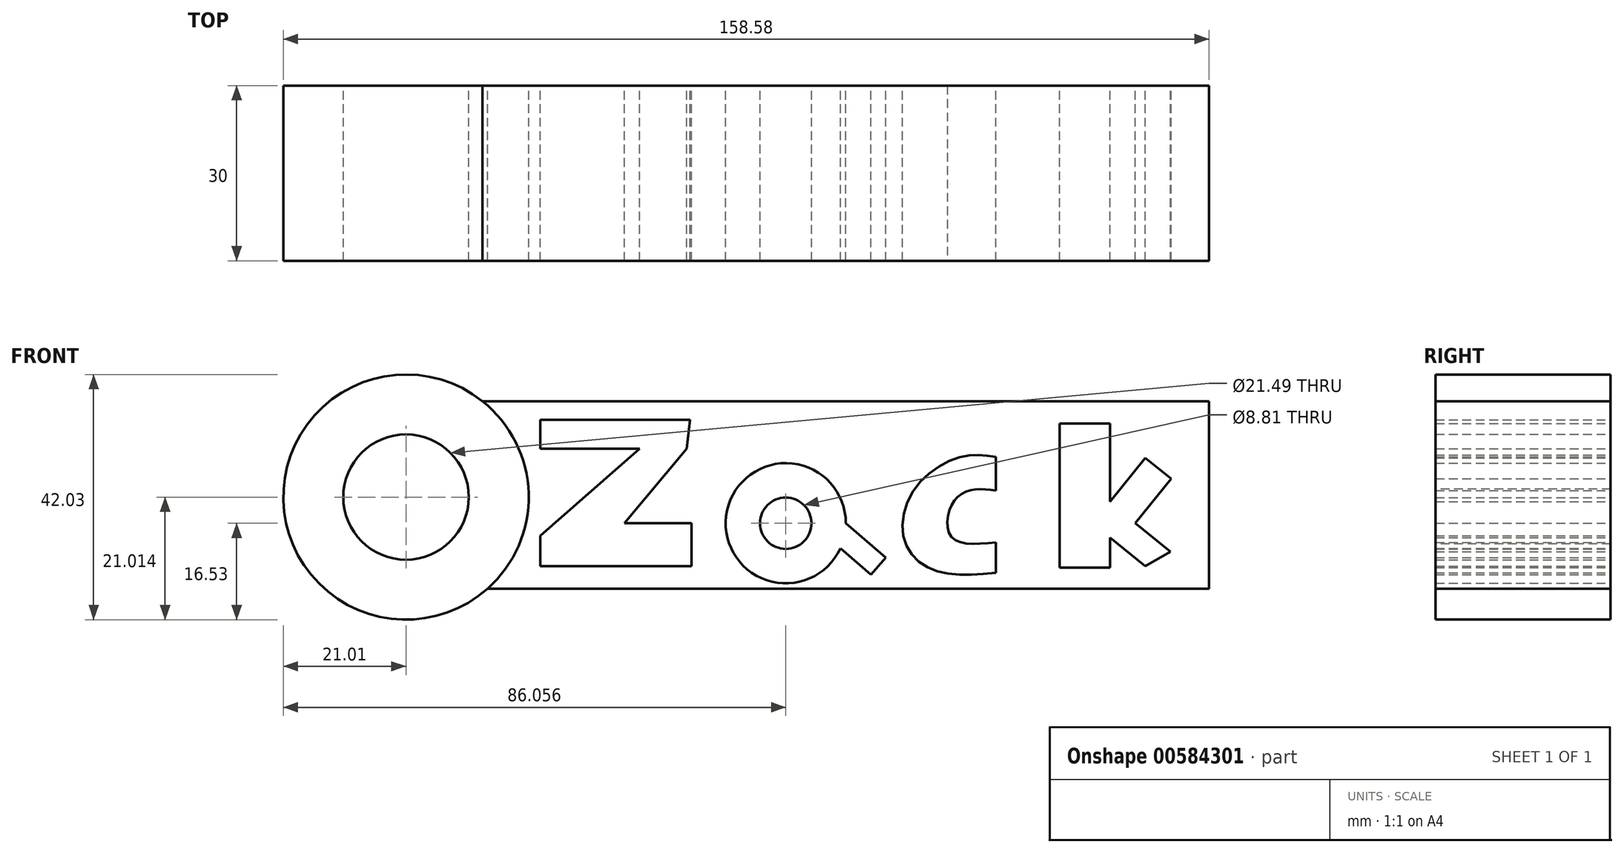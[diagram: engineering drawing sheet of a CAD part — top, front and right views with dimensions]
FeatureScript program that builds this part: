
annotation { "Feature Type Name" : "Feature", "Feature Type Description" : "" }
export const myFeature = defineFeature(function(context is Context, id is Id, definition is map)
    precondition{}
    {
        {
            var Q0;
            Q0=qCreatedBy(makeId("Front.planeOp"),FACE);
            var sketch = newSketch(context, id + "F0", { "sketchPlane" : qUnion([Q0])});
            skCircle(sketch, "E0", {"center": v(-82.17, 4.48) * mm, "radius": 21.01 * mm});
            skCircle(sketch, "E1", {"center": v(-82.17, 4.48) * mm, "radius": 10.75 * mm});
            skLineSegment(sketch, "E2", {"start": v(-69.1, 20.93) * mm, "end": v(55.4, 20.93) * mm});
            skLineSegment(sketch, "E3", {"start": v(-68.2, -11.21) * mm, "end": v(55.4, -11.21) * mm});
            skLineSegment(sketch, "E4", {"start": v(55.4, -11.21) * mm, "end": v(55.4, 20.93) * mm});
            skSolve(sketch);
        }
        {
            var Q0;
            {var subQ0=sQuery(id+"F0.wireOp",EDGE,"E2");Q0=makeQuery(id+"F0.imprint","IMPRINT",FACE,{"disambiguationData":[TD([[makeQuery(id+"F0.imprint","IMPRINT",EDGE,{"derivedFrom":subQ0}),-1.0]])]});}
            var sketch = newSketch(context, id + "F1", { "sketchPlane" : qUnion([Q0])});
            skLineSegment(sketch, "E5", {"start": v(-59.14, 17.7) * mm, "end": v(-59.14, 12.8) * mm});
            skLineSegment(sketch, "E6", {"start": v(-59.14, 12.8) * mm, "end": v(-42.16, 12.8) * mm});
            skLineSegment(sketch, "E7", {"start": v(-42.16, 12.8) * mm, "end": v(-59.14, -2.16) * mm});
            skLineSegment(sketch, "E8", {"start": v(-59.14, -2.16) * mm, "end": v(-59.14, -7.34) * mm});
            skPoint(sketch, "E9.end.orphan", {"position": v(-42.16, 0) * mm});
            skPoint(sketch, "E10.start.orphan", {"position": v(-34.1, 12.8) * mm});
            skPoint(sketch, "E11.end.orphan", {"position": v(-42.16, -7.34) * mm});
            skLineSegment(sketch, "E12", {"start": v(-59.14, -7.34) * mm, "end": v(-33.24, -7.34) * mm});
            skLineSegment(sketch, "E13", {"start": v(-33.24, -7.34) * mm, "end": v(-33.24, 0) * mm});
            skLineSegment(sketch, "E14", {"start": v(-33.24, 0) * mm, "end": v(-44.75, 0) * mm});
            skPoint(sketch, "E15.end.orphan", {"position": v(-30.65, 12.8) * mm});
            skLineSegment(sketch, "E16", {"start": v(-59.14, 17.7) * mm, "end": v(-33.53, 17.7) * mm});
            skLineSegment(sketch, "E17", {"start": v(-33.53, 17.7) * mm, "end": v(-34.1, 12.8) * mm});
            skLineSegment(sketch, "E18", {"start": v(-44.75, 0) * mm, "end": v(-34.1, 12.8) * mm});
            skCircle(sketch, "E19", {"center": v(-17.12, 0) * mm, "radius": 10.3 * mm});
            skCircle(sketch, "E20", {"center": v(-17.12, 0) * mm, "radius": 4.4 * mm});
            skLineSegment(sketch, "E21", {"start": v(-6.83, 0) * mm, "end": v(0, -5.9) * mm});
            skLineSegment(sketch, "E22", {"start": v(0, -5.9) * mm, "end": v(-2.53, -8.83) * mm});
            skLineSegment(sketch, "E23", {"start": v(-2.53, -8.83) * mm, "end": v(-7.77, -4.3) * mm});
            skLineSegment(sketch, "E24", {"start": v(18.85, 11.37) * mm, "end": v(18.85, 5.61) * mm});
            skLineSegment(sketch, "E25", {"start": v(18.85, -3.3) * mm, "end": v(18.85, -8.5) * mm});
            skFitSpline(sketch, "E26", {"points": [v(18.85, 5.61) * mm, v(14.25, 5.61) * mm, v(11.08, 2.73) * mm, v(11.37, -2.45) * mm, v(18.85, -3.3) * mm], "startDerivative": vector(-20.69, 2.65) * mm, "endDerivative": vector(31.06, 2.78) * mm});
            skFitSpline(sketch, "E27", {"points": [v(18.85, 11.37) * mm, v(12.8, 11.37) * mm, v(4.75, 5.61) * mm, v(3.3, -3.3) * mm, v(8.78, -8.2) * mm, v(18.85, -8.5) * mm], "startDerivative": vector(-33.9, 5.02) * mm, "endDerivative": vector(48.74, 4.4) * mm});
            skLineSegment(sketch, "E28", {"start": v(29.79, 17.12) * mm, "end": v(29.79, -7.63) * mm});
            skLineSegment(sketch, "E29", {"start": v(29.79, -7.63) * mm, "end": v(38.42, -7.63) * mm});
            skLineSegment(sketch, "E30", {"start": v(38.42, -7.63) * mm, "end": v(38.42, -2.45) * mm});
            skLineSegment(sketch, "E31", {"start": v(38.42, -2.45) * mm, "end": v(44.47, -7.34) * mm});
            skLineSegment(sketch, "E32", {"start": v(44.47, -7.34) * mm, "end": v(48.78, -4.9) * mm});
            skPoint(sketch, "E32.endSnap0", {"position": v(41.44, -4.9) * mm});
            skLineSegment(sketch, "E33", {"start": v(48.78, -4.9) * mm, "end": v(42.74, 0) * mm});
            skLineSegment(sketch, "E34", {"start": v(42.74, 0) * mm, "end": v(48.9, 7.6) * mm});
            skLineSegment(sketch, "E35", {"start": v(48.9, 7.6) * mm, "end": v(44.47, 11.2) * mm});
            skLineSegment(sketch, "E36", {"start": v(44.47, 11.2) * mm, "end": v(38.42, 3.72) * mm});
            skLineSegment(sketch, "E37", {"start": v(38.42, 3.72) * mm, "end": v(38.42, 17.12) * mm});
            skLineSegment(sketch, "E38", {"start": v(38.42, 17.12) * mm, "end": v(29.5, 17.12) * mm});
            skSolve(sketch);
        }
        {
            var Q0;
            Q0 = qSketchRegion(id + "F1", true);
            var Q1;
            {var subQ0=sQuery(id+"F0.wireOp",EDGE,"E2");Q1=makeQuery(id+"F0.imprint","IMPRINT",FACE,{"disambiguationData":[TD([[makeQuery(id+"F0.imprint","IMPRINT",EDGE,{"derivedFrom":subQ0}),-1.0]])]});}
            extrude(context, id + "F2", {"entities" : qUnion([Q0, Q1]), "depth" : 30 * mm, "offsetDistance" : 25 * mm});
        }
        {
            var Q0;
            Q0 = qSketchRegion(id + "F0", true);
            extrude(context, id + "F3", {"entities" : qUnion([Q0]), "depth" : 30 * mm, "offsetDistance" : 25 * mm});
        }
    });
